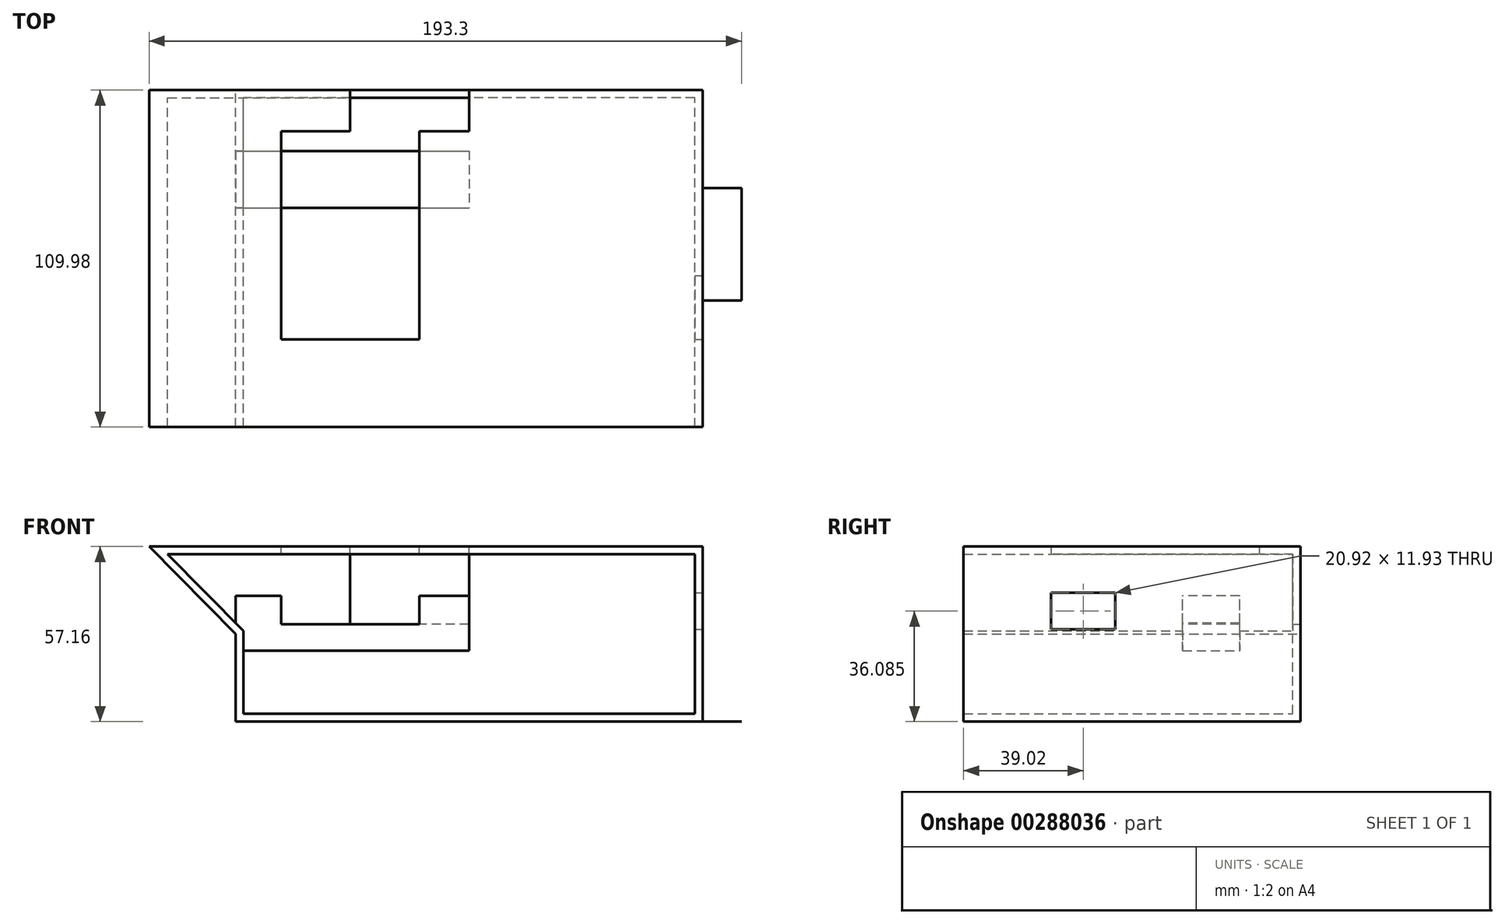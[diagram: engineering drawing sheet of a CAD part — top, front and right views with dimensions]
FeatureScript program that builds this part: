
annotation { "Feature Type Name" : "Feature", "Feature Type Description" : "" }
export const myFeature = defineFeature(function(context is Context, id is Id, definition is map)
    precondition{}
    {
        {
            var Q0;
            Q0=qCreatedBy(makeId("Front.planeOp"),FACE);
            var sketch = newSketch(context, id + "F0", { "sketchPlane" : qUnion([Q0])});
            skLineSegment(sketch, "E0.bottom", {"start": v(76.2, -28.57) * mm, "end": v(-76.2, -28.58) * mm});
            skLineSegment(sketch, "E0.top", {"start": v(76.2, 28.58) * mm, "end": v(-76.2, 28.57) * mm});
            skLineSegment(sketch, "E0.left", {"start": v(76.2, -28.57) * mm, "end": v(76.2, 28.58) * mm});
            skLineSegment(sketch, "E0.right", {"start": v(-76.2, -28.58) * mm, "end": v(-76.2, 28.57) * mm});
            skPoint(sketch, "E0.middle", {"position": v(0, 0) * mm});
            skLineSegment(sketch, "E1.bottom", {"start": v(-76.2, 0) * mm, "end": v(28.2, 0) * mm});
            skLineSegment(sketch, "E1.top", {"start": v(-104.4, 28.58) * mm, "end": v(0, 28.57) * mm});
            skLineSegment(sketch, "E1.left", {"start": v(0, 28.58) * mm, "end": v(28.2, 0) * mm});
            skLineSegment(sketch, "E1.right", {"start": v(-104.4, 28.58) * mm, "end": v(-76.2, 0) * mm});
            skLineSegment(sketch, "E2", {"start": v(-52.2, 28.57) * mm, "end": v(-52.2, -0.77) * mm});
            skSolve(sketch);
        }
        {
            var Q0;
            Q0 = qSketchRegion(id + "F0", true);
            extrude(context, id + "F1", {"entities" : qUnion([Q0]), "endBound" : BoundingType.SYMMETRIC, "depth" : 109.98 * mm});
        }
        {
            var Q0;
            Q0=makeQuery(id+"F1.opExtrude","CAP_FACE",FACE,{"disambiguationData":[OSD([sQuery(id+"F0.wireOp",EDGE,"E0.bottom"),sQuery(id+"F0.wireOp",EDGE,"E0.top"),sQuery(id+"F0.wireOp",EDGE,"E0.left"),sQuery(id+"F0.wireOp",EDGE,"E0.right")])],"isStart":false});
            shell(context, id + "F2", {"entities" : qUnion([Q0]), "thickness" : 2.54 * mm});
        }
        {
            var Q0;
            Q0=qCreatedBy(makeId("Right.planeOp"),FACE);
            var sketch = newSketch(context, id + "F3", { "sketchPlane" : qUnion([Q0])});
            skLineSegment(sketch, "E3.bottom", {"start": v(35.1, -5.44) * mm, "end": v(16.5, -5.44) * mm});
            skLineSegment(sketch, "E3.top", {"start": v(35.1, 12.46) * mm, "end": v(16.5, 12.46) * mm});
            skLineSegment(sketch, "E3.left", {"start": v(35.1, -5.44) * mm, "end": v(35.1, 12.46) * mm});
            skLineSegment(sketch, "E3.right", {"start": v(16.5, -5.44) * mm, "end": v(16.5, 12.46) * mm});
            skSolve(sketch);
        }
        {
            var Q0;
            Q0=makeQuery(id+"F3.imprint","IMPRINT",FACE,{"disambiguationData":[TD([[makeQuery(id+"F3.imprint","IMPRINT",EDGE,{"derivedFrom":sQuery(id+"F3.wireOp",EDGE,"E3.bottom")}),-1.0]])]});
            var Q1;
            Q1=makeQuery(id+"F1.opExtrude","SWEPT_FACE",FACE,{"disambiguationData":[OSD([sQuery(id+"F0.wireOp",EDGE,"E0.right")])]});
            extrude(context, id + "F4", {"entities" : qUnion([Q0]), "operationType" : NewBodyOperationType.ADD, "endBound" : BoundingType.UP_TO_SURFACE, "oppositeDirection" : true, "endBoundEntityFace" : qUnion([Q1]), "depth" : 25.4 * mm});
        }
        {
            var Q0;
            Q0=makeQuery(id+"F1.opExtrude","SWEPT_FACE",FACE,{"disambiguationData":[OSD([sQuery(id+"F0.wireOp",EDGE,"E0.left")])]});
            var sketch = newSketch(context, id + "F5", { "sketchPlane" : qUnion([Q0])});
            skLineSegment(sketch, "E4.bottom", {"start": v(-13.74, -28.58) * mm, "end": v(23, -28.58) * mm});
            skLineSegment(sketch, "E4.top", {"start": v(-13.74, 0) * mm, "end": v(23, 0) * mm});
            skLineSegment(sketch, "E4.left", {"start": v(-13.74, -28.58) * mm, "end": v(-13.74, 0) * mm});
            skLineSegment(sketch, "E4.right", {"start": v(23, -28.58) * mm, "end": v(23, 0) * mm});
            skSolve(sketch);
        }
        {
            var Q0;
            Q0=makeQuery(id+"F5.imprint","IMPRINT",FACE,{"disambiguationData":[TD([[makeQuery(id+"F5.imprint","IMPRINT",EDGE,{"derivedFrom":sQuery(id+"F5.wireOp",EDGE,"E4.bottom")}),1.0]])]});
            extrude(context, id + "F6", {"entities" : qUnion([Q0]), "operationType" : NewBodyOperationType.ADD, "depth" : 12.7 * mm});
        }
        {
            var Q0;
            Q0=makeQuery(id+"F1.opExtrude","SWEPT_FACE",FACE,{"disambiguationData":[OSD([sQuery(id+"F0.wireOp",EDGE,"E0.left")])]});
            var sketch = newSketch(context, id + "F7", { "sketchPlane" : qUnion([Q0])});
            skLineSegment(sketch, "E5.bottom", {"start": v(-26.43, 13.47) * mm, "end": v(-5.51, 13.47) * mm});
            skLineSegment(sketch, "E5.top", {"start": v(-26.43, 1.54) * mm, "end": v(-5.51, 1.54) * mm});
            skLineSegment(sketch, "E5.left", {"start": v(-26.43, 13.47) * mm, "end": v(-26.43, 1.54) * mm});
            skLineSegment(sketch, "E5.right", {"start": v(-5.51, 13.47) * mm, "end": v(-5.51, 1.54) * mm});
            skSolve(sketch);
        }
        {
            var Q0;
            Q0=makeQuery(id+"F7.imprint","IMPRINT",FACE,{"disambiguationData":[TD([[makeQuery(id+"F7.imprint","IMPRINT",EDGE,{"derivedFrom":sQuery(id+"F7.wireOp",EDGE,"E5.bottom")}),-1.0]])]});
            extrude(context, id + "F8", {"entities" : qUnion([Q0]), "operationType" : NewBodyOperationType.REMOVE, "oppositeDirection" : true, "depth" : 25.4 * mm});
        }
        {
            var Q0;
            Q0=makeQuery(id+"F1.opExtrude","SWEPT_FACE",FACE,{"disambiguationData":[OSD([sQuery(id+"F0.wireOp",EDGE,"E0.top")])]});
            var sketch = newSketch(context, id + "F9", { "sketchPlane" : qUnion([Q0])});
            skLineSegment(sketch, "E6", {"start": v(-36.26, 0) * mm, "end": v(-36.26, 23.33) * mm});
            skLineSegment(sketch, "E7", {"start": v(-36.26, 23.33) * mm, "end": v(-75.15, 41.8) * mm});
            skLineSegment(sketch, "E8", {"start": v(-75.15, 41.8) * mm, "end": v(-76.2, 39.6) * mm});
            skSolve(sketch);
        }
        {
            var Q0;
            {var subQ0=sQuery(id+"F0.wireOp",EDGE,"E0.top");var subQ1=makeQuery(id+"F1.opExtrude","CAP_EDGE",EDGE,{"disambiguationData":[OSD([subQ0])],"isStart":true});Q0=makeQuery(id+"F9.imprint","IMPRINT",FACE,{"disambiguationData":[TD([[makeQuery(id+"F9.imprint","IMPRINT",EDGE,{"derivedFrom":subQ1}),1.0]])]});}
            var sketch = newSketch(context, id + "F10", { "sketchPlane" : qUnion([Q0])});
            skLineSegment(sketch, "E9.bottom", {"start": v(-13.52, 0) * mm, "end": v(0, 0) * mm});
            skLineSegment(sketch, "E9.top", {"start": v(-13.52, 0) * mm, "end": v(0, 0) * mm});
            skLineSegment(sketch, "E9.left", {"start": v(-13.52, 0) * mm, "end": v(-13.52, 0) * mm});
            skLineSegment(sketch, "E9.right", {"start": v(0, 0) * mm, "end": v(0, 0) * mm});
            skLineSegment(sketch, "E10.bottom", {"start": v(-16.2, 41.62) * mm, "end": v(-61.37, 41.62) * mm});
            skLineSegment(sketch, "E10.top", {"start": v(-16.2, -26.34) * mm, "end": v(-61.37, -26.34) * mm});
            skLineSegment(sketch, "E10.left", {"start": v(-16.2, 41.62) * mm, "end": v(-16.2, -26.34) * mm});
            skLineSegment(sketch, "E10.right", {"start": v(-61.37, 41.62) * mm, "end": v(-61.37, -26.34) * mm});
            skLineSegment(sketch, "E11.bottom", {"start": v(-38.78, 41.62) * mm, "end": v(0, 41.62) * mm});
            skLineSegment(sketch, "E11.top", {"start": v(-38.78, 97.55) * mm, "end": v(0, 97.55) * mm});
            skLineSegment(sketch, "E11.left", {"start": v(-38.78, 41.62) * mm, "end": v(-38.78, 97.55) * mm});
            skLineSegment(sketch, "E11.right", {"start": v(0, 41.62) * mm, "end": v(0, 97.55) * mm});
            skSolve(sketch);
        }
        {
            var Q0;
            Q0 = qSketchRegion(id + "F10", true);
            extrude(context, id + "F11", {"entities" : qUnion([Q0]), "operationType" : NewBodyOperationType.REMOVE, "oppositeDirection" : true, "depth" : 25.4 * mm});
        }
    });
